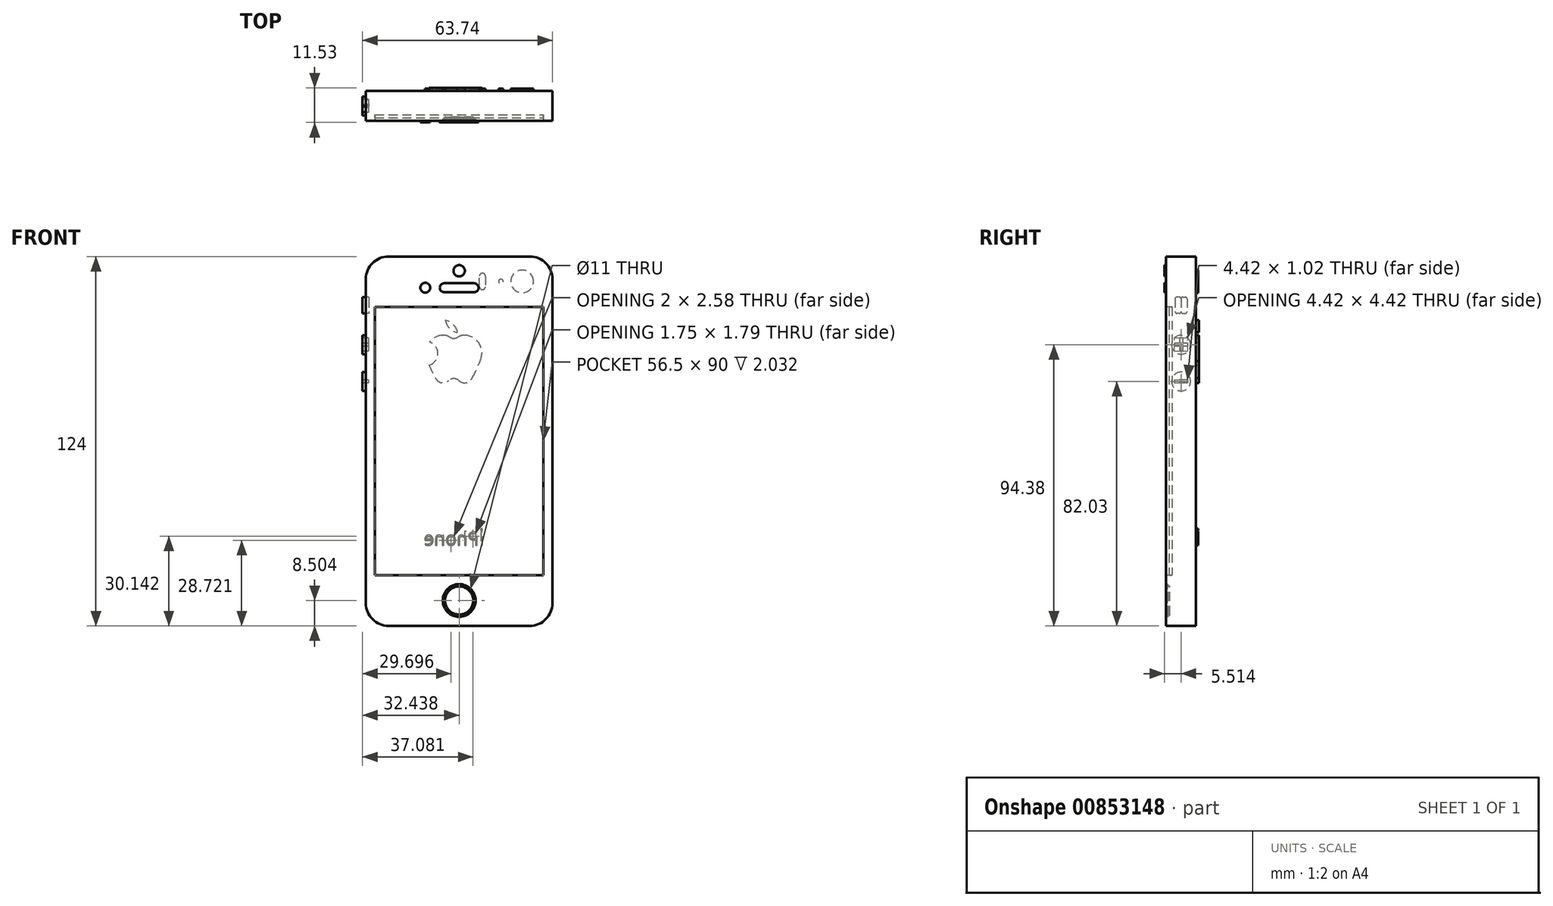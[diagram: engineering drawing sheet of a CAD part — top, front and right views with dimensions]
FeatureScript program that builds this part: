
annotation { "Feature Type Name" : "Feature", "Feature Type Description" : "" }
export const myFeature = defineFeature(function(context is Context, id is Id, definition is map)
    precondition{}
    {
        {
            var Q0;
            Q0=qCreatedBy(makeId("Front.planeOp"),FACE);
            var sketch = newSketch(context, id + "F0", { "sketchPlane" : qUnion([Q0])});
            skLineSegment(sketch, "E0.bottom", {"start": v(-29.5, 62) * mm, "end": v(33.1, 62) * mm});
            skLineSegment(sketch, "E0.top", {"start": v(-29.5, -62) * mm, "end": v(33.1, -62) * mm});
            skLineSegment(sketch, "E0.left", {"start": v(-29.5, 62) * mm, "end": v(-29.5, -62) * mm});
            skLineSegment(sketch, "E0.right", {"start": v(33.1, 62) * mm, "end": v(33.1, -62) * mm});
            skSolve(sketch);
        }
        {
            var Q0;
            Q0=makeQuery(id+"F0.imprint","IMPRINT",FACE,{"disambiguationData":[TD([[makeQuery(id+"F0.imprint","IMPRINT",EDGE,{"derivedFrom":sQuery(id+"F0.wireOp",EDGE,"E0.bottom")}),-1.0]])]});
            extrude(context, id + "F1", {"entities" : qUnion([Q0]), "oppositeDirection" : true, "depth" : 10 * mm, "offsetDistance" : 25.4 * mm});
        }
        {
            var Q0;
            Q0=makeQuery(id+"F1.opExtrude","SWEPT_EDGE",EDGE,{"disambiguationData":[OSD([sQuery(id+"F0.wireOp",EDGE,"E0.bottom"),sQuery(id+"F0.wireOp",EDGE,"E0.right")])]});
            var Q1;
            Q1=makeQuery(id+"F1.opExtrude","SWEPT_EDGE",EDGE,{"disambiguationData":[OSD([sQuery(id+"F0.wireOp",EDGE,"E0.bottom"),sQuery(id+"F0.wireOp",EDGE,"E0.left")])]});
            var Q2;
            Q2=makeQuery(id+"F1.opExtrude","SWEPT_EDGE",EDGE,{"disambiguationData":[OSD([sQuery(id+"F0.wireOp",EDGE,"E0.top"),sQuery(id+"F0.wireOp",EDGE,"E0.right")])]});
            var Q3;
            Q3=makeQuery(id+"F1.opExtrude","SWEPT_EDGE",EDGE,{"disambiguationData":[OSD([sQuery(id+"F0.wireOp",EDGE,"E0.top"),sQuery(id+"F0.wireOp",EDGE,"E0.left")])]});
            fillet(context, id + "F2", {"entities" : qUnion([Q0, Q1, Q2, Q3]), "radius" : 7.62 * mm, "tangentPropagation" : true, "allowEdgeOverflow" : false});
        }
        {
            var Q0;
            Q0=makeQuery(id+"F1.opExtrude","CAP_FACE",FACE,{"disambiguationData":[OSD([sQuery(id+"F0.wireOp",EDGE,"E0.bottom"),sQuery(id+"F0.wireOp",EDGE,"E0.top"),sQuery(id+"F0.wireOp",EDGE,"E0.left"),sQuery(id+"F0.wireOp",EDGE,"E0.right")])],"isStart":true});
            var sketch = newSketch(context, id + "F3", { "sketchPlane" : qUnion([Q0])});
            skLineSegment(sketch, "E1.bottom", {"start": v(-26.45, 45) * mm, "end": v(30.05, 45) * mm});
            skLineSegment(sketch, "E1.top", {"start": v(-26.45, -45) * mm, "end": v(30.05, -45) * mm});
            skLineSegment(sketch, "E1.left", {"start": v(-26.45, 45) * mm, "end": v(-26.45, -45) * mm});
            skLineSegment(sketch, "E1.right", {"start": v(30.05, 45) * mm, "end": v(30.05, -45) * mm});
            skSolve(sketch);
        }
        {
            var Q0;
            Q0=makeQuery(id+"F3.imprint","IMPRINT",FACE,{"disambiguationData":[TD([[makeQuery(id+"F3.imprint","IMPRINT",EDGE,{"derivedFrom":sQuery(id+"F3.wireOp",EDGE,"E1.bottom")}),-1.0]])]});
            extrude(context, id + "F4", {"entities" : qUnion([Q0]), "operationType" : NewBodyOperationType.REMOVE, "oppositeDirection" : true, "depth" : 2.03 * mm, "offsetDistance" : 25.4 * mm});
        }
        {
            var Q0;
            Q0=makeQuery(id+"F1.opExtrude","CAP_FACE",FACE,{"disambiguationData":[OSD([sQuery(id+"F0.wireOp",EDGE,"E0.bottom"),sQuery(id+"F0.wireOp",EDGE,"E0.top"),sQuery(id+"F0.wireOp",EDGE,"E0.left"),sQuery(id+"F0.wireOp",EDGE,"E0.right")])],"isStart":true});
            var sketch = newSketch(context, id + "F5", { "sketchPlane" : qUnion([Q0])});
            skCircle(sketch, "E2", {"center": v(1.8, -53.5) * mm, "radius": 5.5 * mm});
            skPoint(sketch, "E2.centerSnap0", {"position": v(1.8, -45) * mm});
            skSolve(sketch);
        }
        {
            var Q0;
            Q0=makeQuery(id+"F5.imprint","IMPRINT",FACE,{"disambiguationData":[TD([[makeQuery(id+"F5.imprint","IMPRINT",EDGE,{"derivedFrom":sQuery(id+"F5.wireOp",EDGE,"E2")}),1.0]])]});
            extrude(context, id + "F6", {"entities" : qUnion([Q0]), "operationType" : NewBodyOperationType.REMOVE, "oppositeDirection" : true, "depth" : 1.27 * mm, "offsetDistance" : 25.4 * mm});
        }
        {
            var Q0;
            Q0=makeQuery(id+"F6.boolean.opBoolean","COPY",EDGE,{"derivedFrom":makeQuery(id+"F6.opExtrude","CAP_EDGE",EDGE,{"disambiguationData":[OSD([sQuery(id+"F5.wireOp",EDGE,"E2")])],"isStart":false})});
            chamfer(context, id + "F7", {"entities" : qUnion([Q0]), "width" : 0.76 * mm, "tangentPropagation" : true});
        }
        {
            var Q0;
            Q0=makeQuery(id+"F1.opExtrude","CAP_FACE",FACE,{"disambiguationData":[OSD([sQuery(id+"F0.wireOp",EDGE,"E0.bottom"),sQuery(id+"F0.wireOp",EDGE,"E0.top"),sQuery(id+"F0.wireOp",EDGE,"E0.left"),sQuery(id+"F0.wireOp",EDGE,"E0.right")])],"isStart":true});
            var sketch = newSketch(context, id + "F8", { "sketchPlane" : qUnion([Q0])});
            skCircle(sketch, "E3", {"center": v(1.8, 57.2) * mm, "radius": 1.9 * mm});
            skPoint(sketch, "E3.centerSnap0", {"position": v(1.8, 45) * mm});
            skArc(sketch, "E4", {"start": v(-3.2, 53) * mm, "mid": v(-4.7, 51.5) * mm, "end": v(-3.2, 50) * mm});
            skArc(sketch, "E5", {"start": v(6.8, 50) * mm, "mid": v(8.3, 51.5) * mm, "end": v(6.8, 53) * mm});
            skLineSegment(sketch, "E6", {"start": v(-3.2, 53) * mm, "end": v(6.8, 53) * mm});
            skLineSegment(sketch, "E7", {"start": v(6.8, 50) * mm, "end": v(-3.2, 50) * mm});
            skCircle(sketch, "E8", {"center": v(-9.55, 51.5) * mm, "radius": 1.65 * mm});
            skSolve(sketch);
        }
        {
            var Q0;
            Q0=makeQuery(id+"F8.imprint","IMPRINT",FACE,{"disambiguationData":[TD([[makeQuery(id+"F8.imprint","IMPRINT",EDGE,{"derivedFrom":sQuery(id+"F8.wireOp",EDGE,"E8")}),1.0]])]});
            var Q1;
            Q1=makeQuery(id+"F8.imprint","IMPRINT",FACE,{"disambiguationData":[TD([[makeQuery(id+"F8.imprint","IMPRINT",EDGE,{"derivedFrom":sQuery(id+"F8.wireOp",EDGE,"E4")}),1.0]])]});
            var Q2;
            Q2=makeQuery(id+"F8.imprint","IMPRINT",FACE,{"disambiguationData":[TD([[makeQuery(id+"F8.imprint","IMPRINT",EDGE,{"derivedFrom":sQuery(id+"F8.wireOp",EDGE,"E3")}),1.0]])]});
            extrude(context, id + "F9", {"entities" : qUnion([Q0, Q1, Q2]), "depth" : 0.5 * mm, "offsetDistance" : 25.4 * mm});
        }
        {
            var Q0;
            Q0=makeQuery(id+"F1.opExtrude","SWEPT_FACE",FACE,{"disambiguationData":[OSD([sQuery(id+"F0.wireOp",EDGE,"E0.left")])]});
            var sketch = newSketch(context, id + "F10", { "sketchPlane" : qUnion([Q0])});
            skCircle(sketch, "E9", {"center": v(-5, 20.03) * mm, "radius": 3.18 * mm});
            skCircle(sketch, "E10", {"center": v(-5, 32.38) * mm, "radius": 3.18 * mm});
            skLineSegment(sketch, "E11.bottom", {"start": v(-5, 48.38) * mm, "end": v(-3, 48.38) * mm});
            skLineSegment(sketch, "E11.top", {"start": v(-5, 42.88) * mm, "end": v(-3, 42.88) * mm});
            skLineSegment(sketch, "E11.left", {"start": v(-5, 48.38) * mm, "end": v(-5, 42.88) * mm});
            skLineSegment(sketch, "E11.right", {"start": v(-3, 48.38) * mm, "end": v(-3, 42.88) * mm});
            skLineSegment(sketch, "E12.bottom", {"start": v(-5, 48.38) * mm, "end": v(-7.01, 48.38) * mm});
            skLineSegment(sketch, "E12.top", {"start": v(-5, 42.88) * mm, "end": v(-7.01, 42.88) * mm});
            skLineSegment(sketch, "E12.right", {"start": v(-7.01, 48.38) * mm, "end": v(-7.01, 42.88) * mm});
            skSolve(sketch);
        }
        {
            var Q0;
            Q0=makeQuery(id+"F10.imprint","IMPRINT",FACE,{"disambiguationData":[TD([[makeQuery(id+"F10.imprint","IMPRINT",EDGE,{"derivedFrom":sQuery(id+"F10.wireOp",EDGE,"E10")}),1.0]])]});
            var Q1;
            Q1=makeQuery(id+"F10.imprint","IMPRINT",FACE,{"disambiguationData":[TD([[makeQuery(id+"F10.imprint","IMPRINT",EDGE,{"derivedFrom":sQuery(id+"F10.wireOp",EDGE,"E9")}),1.0]])]});
            var Q2;
            Q2=makeQuery(id+"F10.imprint","IMPRINT",FACE,{"disambiguationData":[TD([[makeQuery(id+"F10.imprint","IMPRINT",EDGE,{"derivedFrom":sQuery(id+"F10.wireOp",EDGE,"E11.bottom")}),-1.0]])]});
            extrude(context, id + "F11", {"entities" : qUnion([Q0, Q1, Q2]), "depth" : 1.14 * mm, "offsetDistance" : 25.4 * mm});
        }
        {
            var Q0;
            Q0=makeQuery(id+"F10.imprint","IMPRINT",FACE,{"disambiguationData":[TD([[makeQuery(id+"F10.imprint","IMPRINT",EDGE,{"derivedFrom":sQuery(id+"F10.wireOp",EDGE,"E12.bottom")}),1.0]])]});
            extrude(context, id + "F12", {"entities" : qUnion([Q0]), "operationType" : NewBodyOperationType.REMOVE, "oppositeDirection" : true, "depth" : 1.02 * mm, "offsetDistance" : 25.4 * mm});
        }
        {
            var Q0;
            Q0=makeQuery(id+"F11.opExtrude","SWEPT_EDGE",EDGE,{"disambiguationData":[OSD([sQuery(id+"F10.wireOp",EDGE,"E11.bottom"),sQuery(id+"F10.wireOp",EDGE,"E12.bottom"),sQuery(id+"F10.wireOp",EDGE,"E11.left")])]});
            var Q1;
            Q1=makeQuery(id+"F11.opExtrude","SWEPT_EDGE",EDGE,{"disambiguationData":[OSD([sQuery(id+"F10.wireOp",EDGE,"E11.bottom"),sQuery(id+"F10.wireOp",EDGE,"E11.right")])]});
            var Q2;
            Q2=makeQuery(id+"F11.opExtrude","SWEPT_EDGE",EDGE,{"disambiguationData":[OSD([sQuery(id+"F10.wireOp",EDGE,"E11.top"),sQuery(id+"F10.wireOp",EDGE,"E12.top"),sQuery(id+"F10.wireOp",EDGE,"E11.left")])]});
            var Q3;
            Q3=makeQuery(id+"F11.opExtrude","SWEPT_EDGE",EDGE,{"disambiguationData":[OSD([sQuery(id+"F10.wireOp",EDGE,"E11.top"),sQuery(id+"F10.wireOp",EDGE,"E11.right")])]});
            fillet(context, id + "F13", {"entities" : qUnion([Q0, Q1, Q2, Q3]), "radius" : 0.64 * mm, "tangentPropagation" : true, "allowEdgeOverflow" : false});
        }
        {
            var Q0;
            Q0=makeQuery(id+"F12.boolean.opBoolean","COPY",EDGE,{"derivedFrom":makeQuery(id+"F12.opExtrude","SWEPT_EDGE",EDGE,{"disambiguationData":[OSD([sQuery(id+"F10.wireOp",EDGE,"E12.top"),sQuery(id+"F10.wireOp",EDGE,"E12.right")])]})});
            var Q1;
            Q1=makeQuery(id+"F12.boolean.opBoolean","COPY",EDGE,{"derivedFrom":makeQuery(id+"F12.opExtrude","SWEPT_EDGE",EDGE,{"disambiguationData":[OSD([sQuery(id+"F10.wireOp",EDGE,"E11.top"),sQuery(id+"F10.wireOp",EDGE,"E12.top"),sQuery(id+"F10.wireOp",EDGE,"E11.left")])]})});
            var Q2;
            Q2=makeQuery(id+"F12.boolean.opBoolean","COPY",EDGE,{"derivedFrom":makeQuery(id+"F12.opExtrude","SWEPT_EDGE",EDGE,{"disambiguationData":[OSD([sQuery(id+"F10.wireOp",EDGE,"E11.bottom"),sQuery(id+"F10.wireOp",EDGE,"E12.bottom"),sQuery(id+"F10.wireOp",EDGE,"E11.left")])]})});
            var Q3;
            Q3=makeQuery(id+"F12.boolean.opBoolean","COPY",EDGE,{"derivedFrom":makeQuery(id+"F12.opExtrude","SWEPT_EDGE",EDGE,{"disambiguationData":[OSD([sQuery(id+"F10.wireOp",EDGE,"E12.bottom"),sQuery(id+"F10.wireOp",EDGE,"E12.right")])]})});
            fillet(context, id + "F14", {"entities" : qUnion([Q0, Q1, Q2, Q3]), "radius" : 0.64 * mm, "tangentPropagation" : true, "allowEdgeOverflow" : false});
        }
        {
            var Q0;
            Q0=makeQuery(id+"F11.opExtrude","CAP_FACE",FACE,{"disambiguationData":[OSD([sQuery(id+"F10.wireOp",EDGE,"E10")])],"isStart":false});
            var sketch = newSketch(context, id + "F15", { "sketchPlane" : qUnion([Q0])});
            skLineSegment(sketch, "E13.bottom", {"start": v(-7.21, 20.54) * mm, "end": v(-2.8, 20.54) * mm});
            skLineSegment(sketch, "E13.top", {"start": v(-7.21, 19.52) * mm, "end": v(-2.8, 19.52) * mm});
            skLineSegment(sketch, "E13.left", {"start": v(-7.21, 20.54) * mm, "end": v(-7.21, 19.52) * mm});
            skLineSegment(sketch, "E13.right", {"start": v(-2.8, 20.54) * mm, "end": v(-2.8, 19.52) * mm});
            skLineSegment(sketch, "E14.bottom", {"start": v(-5.51, 34.59) * mm, "end": v(-4.5, 34.59) * mm});
            skLineSegment(sketch, "E14.top", {"start": v(-5.51, 30.17) * mm, "end": v(-4.5, 30.17) * mm});
            skLineSegment(sketch, "E14.left", {"start": v(-5.51, 34.59) * mm, "end": v(-5.51, 32.89) * mm});
            skLineSegment(sketch, "E14.right", {"start": v(-4.5, 34.59) * mm, "end": v(-4.5, 32.89) * mm});
            skLineSegment(sketch, "E15.bottom", {"start": v(-7.21, 32.89) * mm, "end": v(-5.51, 32.89) * mm});
            skLineSegment(sketch, "E15.top", {"start": v(-7.21, 31.87) * mm, "end": v(-5.51, 31.87) * mm});
            skLineSegment(sketch, "E15.left", {"start": v(-7.21, 32.89) * mm, "end": v(-7.21, 31.87) * mm});
            skLineSegment(sketch, "E15.right", {"start": v(-2.8, 32.89) * mm, "end": v(-2.8, 31.87) * mm});
            skPoint(sketch, "E16.center.orphan", {"position": v(-5, 32.38) * mm});
            skPoint(sketch, "E17.center.orphan", {"position": v(-5, 20.03) * mm});
            skLineSegment(sketch, "E18.trimOffspring", {"start": v(-5.51, 31.87) * mm, "end": v(-5.51, 30.17) * mm});
            skLineSegment(sketch, "E19.trimOffspring", {"start": v(-4.5, 32.89) * mm, "end": v(-2.8, 32.89) * mm});
            skLineSegment(sketch, "E20.trimOffspring", {"start": v(-4.5, 31.87) * mm, "end": v(-4.5, 30.17) * mm});
            skLineSegment(sketch, "E21.trimOffspring", {"start": v(-4.5, 31.87) * mm, "end": v(-2.8, 31.87) * mm});
            skSolve(sketch);
        }
        {
            var Q0;
            Q0=makeQuery(id+"F15.imprint","IMPRINT",FACE,{"disambiguationData":[TD([[makeQuery(id+"F15.imprint","IMPRINT",EDGE,{"derivedFrom":sQuery(id+"F15.wireOp",EDGE,"E14.bottom")}),-1.0]])]});
            var Q1;
            Q1=makeQuery(id+"F15.imprint","IMPRINT",FACE,{"disambiguationData":[TD([[makeQuery(id+"F15.imprint","IMPRINT",EDGE,{"derivedFrom":sQuery(id+"F15.wireOp",EDGE,"E13.bottom")}),-1.0]])]});
            extrude(context, id + "F16", {"entities" : qUnion([Q0, Q1]), "operationType" : NewBodyOperationType.REMOVE, "oppositeDirection" : true, "depth" : 2.03 * mm, "offsetDistance" : 25.4 * mm});
        }
        {
            var Q0;
            Q0=makeQuery(id+"F1.opExtrude","CAP_FACE",FACE,{"disambiguationData":[OSD([sQuery(id+"F0.wireOp",EDGE,"E0.bottom"),sQuery(id+"F0.wireOp",EDGE,"E0.top"),sQuery(id+"F0.wireOp",EDGE,"E0.left"),sQuery(id+"F0.wireOp",EDGE,"E0.right")])],"isStart":false});
            var sketch = newSketch(context, id + "F17", { "sketchPlane" : qUnion([Q0])});
            skLineSegment(sketch, "E22.bottom", {"start": v(-3.75, 35.56) * mm, "end": v(-3.6, 35.56) * mm});
            skArc(sketch, "E23", {"start": v(-6.15, 21.21) * mm, "mid": v(-4.14, 19.61) * mm, "end": v(-1.67, 20.34) * mm});
            skArc(sketch, "E24", {"start": v(-1.3, 34.89) * mm, "mid": v(-2.4, 35.39) * mm, "end": v(-3.6, 35.56) * mm});
            skArc(sketch, "E25", {"start": v(-3.75, 35.56) * mm, "mid": v(-8.6, 32.6) * mm, "end": v(-8.78, 26.92) * mm});
            skArc(sketch, "E26", {"start": v(-8.78, 26.92) * mm, "mid": v(-7.63, 24) * mm, "end": v(-6.15, 21.21) * mm});
            skArc(sketch, "E27.MirrorC", {"start": v(3.75, 35.56) * mm, "mid": v(8.6, 32.6) * mm, "end": v(8.78, 26.92) * mm});
            skArc(sketch, "E28.MirrorC", {"start": v(1.3, 34.89) * mm, "mid": v(2.4, 35.39) * mm, "end": v(3.6, 35.56) * mm});
            skArc(sketch, "E29.MirrorC", {"start": v(6.15, 21.21) * mm, "mid": v(4.14, 19.61) * mm, "end": v(1.67, 20.34) * mm});
            skArc(sketch, "E30.MirrorCS", {"start": v(8.78, 26.92) * mm, "mid": v(7.63, 24) * mm, "end": v(6.15, 21.21) * mm});
            skLineSegment(sketch, "E31.MirrorCS", {"start": v(3.75, 35.56) * mm, "end": v(3.6, 35.56) * mm});
            skArc(sketch, "E32", {"start": v(-1.3, 34.89) * mm, "mid": v(0, 34.51) * mm, "end": v(1.3, 34.89) * mm});
            skArc(sketch, "E33", {"start": v(1.67, 20.34) * mm, "mid": v(0, 21) * mm, "end": v(-1.67, 20.34) * mm});
            skArc(sketch, "E34", {"start": v(2.81, 40.55) * mm, "mid": v(0.16, 39.15) * mm, "end": v(-1.25, 36.5) * mm});
            skArc(sketch, "E35", {"start": v(-1.25, 36.5) * mm, "mid": v(1.41, 37.9) * mm, "end": v(2.81, 40.55) * mm});
            skSolve(sketch);
        }
        {
            var Q0;
            Q0=makeQuery(id+"F17.imprint","IMPRINT",FACE,{"disambiguationData":[TD([[makeQuery(id+"F17.imprint","IMPRINT",EDGE,{"derivedFrom":sQuery(id+"F17.wireOp",EDGE,"E22.bottom")}),-1.0]])]});
            var Q1;
            Q1=makeQuery(id+"F17.imprint","IMPRINT",FACE,{"disambiguationData":[TD([[makeQuery(id+"F17.imprint","IMPRINT",EDGE,{"derivedFrom":sQuery(id+"F17.wireOp",EDGE,"E34")}),1.0]])]});
            extrude(context, id + "F18", {"entities" : qUnion([Q0, Q1]), "depth" : 1.02 * mm, "offsetDistance" : 25.4 * mm});
        }
        {
            var Q0;
            Q0=makeQuery(id+"F18.opExtrude","CAP_FACE",FACE,{"disambiguationData":[OSD([sQuery(id+"F17.wireOp",EDGE,"E22.bottom"),sQuery(id+"F17.wireOp",EDGE,"E23"),sQuery(id+"F17.wireOp",EDGE,"E24"),sQuery(id+"F17.wireOp",EDGE,"E25"),sQuery(id+"F17.wireOp",EDGE,"E26"),sQuery(id+"F17.wireOp",EDGE,"E27.MirrorC"),sQuery(id+"F17.wireOp",EDGE,"E28.MirrorC"),sQuery(id+"F17.wireOp",EDGE,"E29.MirrorC"),sQuery(id+"F17.wireOp",EDGE,"E30.MirrorCS"),sQuery(id+"F17.wireOp",EDGE,"E31.MirrorCS"),sQuery(id+"F17.wireOp",EDGE,"E32"),sQuery(id+"F17.wireOp",EDGE,"E33")])],"isStart":false});
            var sketch = newSketch(context, id + "F19", { "sketchPlane" : qUnion([Q0])});
            skCircle(sketch, "E36", {"center": v(9.4, 29.43) * mm, "radius": 4.06 * mm});
            skSolve(sketch);
        }
        {
            var Q0;
            {var subQ0=sQuery(id+"F19.wireOp",EDGE,"E36");var subQ1=makeQuery(id+"F18.opExtrude","CAP_EDGE",EDGE,{"disambiguationData":[OSD([sQuery(id+"F17.wireOp",EDGE,"E27.MirrorC")])],"isStart":false});var subQ2=makeQuery(id+"F19.imprint","INTERSECT",VERTEX,{"derivedFrom":[subQ1,subQ0]});Q0=makeQuery(id+"F19.imprint","IMPRINT",FACE,{"disambiguationData":[TD([[makeQuery(id+"F19.imprint","IMPRINT",EDGE,{"disambiguationData":[TD([[subQ2,-1.0]])],"derivedFrom":subQ0}),1.0]])]});}
            extrude(context, id + "F20", {"entities" : qUnion([Q0]), "operationType" : NewBodyOperationType.REMOVE, "oppositeDirection" : true, "depth" : 1.02 * mm, "offsetDistance" : 25.4 * mm});
        }
        {
            var Q0;
            Q0=makeQuery(id+"F1.opExtrude","CAP_FACE",FACE,{"disambiguationData":[OSD([sQuery(id+"F0.wireOp",EDGE,"E0.bottom"),sQuery(id+"F0.wireOp",EDGE,"E0.top"),sQuery(id+"F0.wireOp",EDGE,"E0.left"),sQuery(id+"F0.wireOp",EDGE,"E0.right")])],"isStart":false});
            var sketch = newSketch(context, id + "F21", { "sketchPlane" : qUnion([Q0])});
            skCircle(sketch, "E37", {"center": v(-22.94, 53.62) * mm, "radius": 3.81 * mm});
            skCircle(sketch, "E38", {"center": v(-15.82, 53.62) * mm, "radius": 0.76 * mm});
            skArc(sketch, "E39", {"start": v(-8.6, 55.4) * mm, "mid": v(-9.6, 56.4) * mm, "end": v(-10.6, 55.4) * mm});
            skArc(sketch, "E40", {"start": v(-10.6, 51.84) * mm, "mid": v(-9.6, 50.85) * mm, "end": v(-8.6, 51.84) * mm});
            skLineSegment(sketch, "E41", {"start": v(-10.6, 55.4) * mm, "end": v(-10.6, 51.84) * mm});
            skLineSegment(sketch, "E42", {"start": v(-8.6, 51.84) * mm, "end": v(-8.6, 55.4) * mm});
            skPoint(sketch, "E43", {"position": v(-10.6, 53.62) * mm});
            skSolve(sketch);
        }
        {
            var Q0;
            Q0=makeQuery(id+"F21.imprint","IMPRINT",FACE,{"disambiguationData":[TD([[makeQuery(id+"F21.imprint","IMPRINT",EDGE,{"derivedFrom":sQuery(id+"F21.wireOp",EDGE,"E37")}),1.0]])]});
            var Q1;
            Q1=makeQuery(id+"F21.imprint","IMPRINT",FACE,{"disambiguationData":[TD([[makeQuery(id+"F21.imprint","IMPRINT",EDGE,{"derivedFrom":sQuery(id+"F21.wireOp",EDGE,"E38")}),1.0]])]});
            extrude(context, id + "F22", {"entities" : qUnion([Q0, Q1]), "depth" : 0.76 * mm, "offsetDistance" : 25.4 * mm});
        }
        {
            var Q0;
            Q0=makeQuery(id+"F21.imprint","IMPRINT",FACE,{"disambiguationData":[TD([[makeQuery(id+"F21.imprint","IMPRINT",EDGE,{"derivedFrom":sQuery(id+"F21.wireOp",EDGE,"E39")}),1.0]])]});
            extrude(context, id + "F23", {"entities" : qUnion([Q0]), "depth" : 0.76 * mm, "offsetDistance" : 25.4 * mm});
        }
        {
            var Q0;
            Q0=makeQuery(id+"F4.boolean.opBoolean","COPY",FACE,{"derivedFrom":makeQuery(id+"F4.opExtrude","CAP_FACE",FACE,{"disambiguationData":[OSD([sQuery(id+"F3.wireOp",EDGE,"E1.bottom"),sQuery(id+"F3.wireOp",EDGE,"E1.top"),sQuery(id+"F3.wireOp",EDGE,"E1.left"),sQuery(id+"F3.wireOp",EDGE,"E1.right")])],"isStart":false})});
            var sketch = newSketch(context, id + "F24", { "sketchPlane" : qUnion([Q0])});
            skLineSegment(sketch, "E44.bottom", {"start": v(-26.45, 45) * mm, "end": v(30.05, 45) * mm});
            skLineSegment(sketch, "E44.top", {"start": v(-26.45, -45) * mm, "end": v(30.05, -45) * mm});
            skLineSegment(sketch, "E44.left", {"start": v(-26.45, 45) * mm, "end": v(-26.45, -45) * mm});
            skLineSegment(sketch, "E44.right", {"start": v(30.05, 45) * mm, "end": v(30.05, -45) * mm});
            skSolve(sketch);
        }
        {
            var Q0;
            Q0=makeQuery(id+"F24.imprint","IMPRINT",FACE,{"disambiguationData":[TD([[makeQuery(id+"F24.imprint","IMPRINT",EDGE,{"derivedFrom":sQuery(id+"F24.wireOp",EDGE,"E44.bottom")}),-1.0]])]});
            extrude(context, id + "F25", {"entities" : qUnion([Q0]), "depth" : 1.02 * mm, "offsetDistance" : 25.4 * mm});
        }
        {
            var Q0;
            Q0=makeQuery(id+"F6.boolean.opBoolean","COPY",FACE,{"derivedFrom":makeQuery(id+"F6.opExtrude","CAP_FACE",FACE,{"disambiguationData":[OSD([sQuery(id+"F5.wireOp",EDGE,"E2")])],"isStart":false})});
            var sketch = newSketch(context, id + "F26", { "sketchPlane" : qUnion([Q0])});
            skCircle(sketch, "E45", {"center": v(1.8, -53.5) * mm, "radius": 4.74 * mm});
            skSolve(sketch);
        }
        {
            var Q0;
            Q0=makeQuery(id+"F26.imprint","IMPRINT",FACE,{"disambiguationData":[TD([[makeQuery(id+"F26.imprint","IMPRINT",EDGE,{"derivedFrom":sQuery(id+"F26.wireOp",EDGE,"E45")}),1.0]])]});
            extrude(context, id + "F27", {"entities" : qUnion([Q0]), "depth" : 0.5 * mm, "offsetDistance" : 25.4 * mm});
        }
        {
            var Q0;
            Q0=makeQuery(id+"F1.opExtrude","CAP_FACE",FACE,{"disambiguationData":[OSD([sQuery(id+"F0.wireOp",EDGE,"E0.bottom"),sQuery(id+"F0.wireOp",EDGE,"E0.top"),sQuery(id+"F0.wireOp",EDGE,"E0.left"),sQuery(id+"F0.wireOp",EDGE,"E0.right")])],"isStart":false});
            var sketch = newSketch(context, id + "F28", { "sketchPlane" : qUnion([Q0])});
            skText(sketch, "E46", { "text": "İPhone", "fontName": "OpenSans-Regular.ttf"});
            const initialGuessF28  = {"E46": [-0.01016, -0.03493, 1, 0, 0.00445]};
            skSetInitialGuess(sketch, initialGuessF28);
            skSolve(sketch);
        }
        {
            var Q0;
            Q0 = qSketchRegion(id + "F28", true);
            extrude(context, id + "F29", {"entities" : qUnion([Q0]), "depth" : 0.76 * mm, "offsetDistance" : 25.4 * mm});
        }
    });
